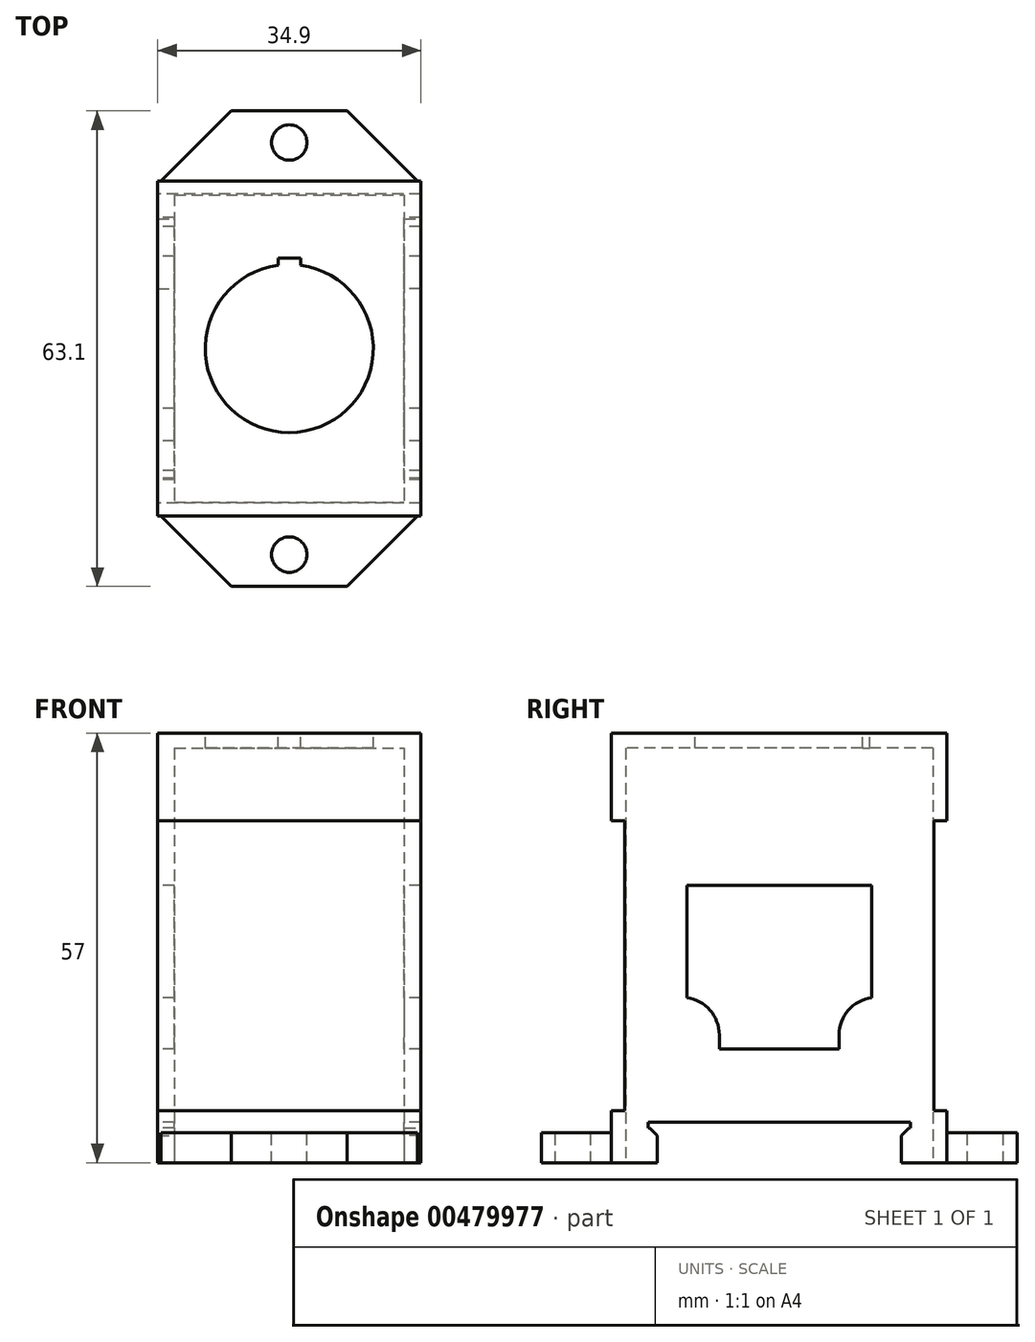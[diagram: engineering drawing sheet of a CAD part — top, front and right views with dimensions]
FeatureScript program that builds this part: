
annotation { "Feature Type Name" : "Feature", "Feature Type Description" : "" }
export const myFeature = defineFeature(function(context is Context, id is Id, definition is map)
    precondition{}
    {
        {
            var Q0;
            Q0=qCreatedBy(makeId("Top.planeOp"),FACE);
            var sketch = newSketch(context, id + "F0", { "sketchPlane" : qUnion([Q0])});
            skLineSegment(sketch, "E0.bottom", {"start": v(0, 0.4) * mm, "end": v(34.9, 0.4) * mm});
            skLineSegment(sketch, "E0.top", {"start": v(0, 44.9) * mm, "end": v(34.9, 44.9) * mm});
            skLineSegment(sketch, "E0.left", {"start": v(0, 0.4) * mm, "end": v(0, 44.9) * mm});
            skLineSegment(sketch, "E0.right", {"start": v(34.9, 0.4) * mm, "end": v(34.9, 44.9) * mm});
            skSolve(sketch);
        }
        {
            var Q0;
            Q0 = qSketchRegion(id + "F0", true);
            extrude(context, id + "F1", {"entities" : qUnion([Q0]), "depth" : 57 * mm});
        }
        {
            var Q0;
            Q0=makeQuery(id+"F1.opExtrude","CAP_FACE",FACE,{"disambiguationData":[OSD([sQuery(id+"F0.wireOp",EDGE,"E0.bottom"),sQuery(id+"F0.wireOp",EDGE,"E0.top"),sQuery(id+"F0.wireOp",EDGE,"E0.left"),sQuery(id+"F0.wireOp",EDGE,"E0.right")])],"isStart":true});
            var sketch = newSketch(context, id + "F2", { "sketchPlane" : qUnion([Q0])});
            skLineSegment(sketch, "E1.bottom", {"start": v(2.2, -43.06) * mm, "end": v(32.7, -43.06) * mm});
            skLineSegment(sketch, "E1.top", {"start": v(2.2, -2.26) * mm, "end": v(32.7, -2.26) * mm});
            skLineSegment(sketch, "E1.left", {"start": v(2.2, -43.06) * mm, "end": v(2.2, -2.26) * mm});
            skLineSegment(sketch, "E1.right", {"start": v(32.7, -43.06) * mm, "end": v(32.7, -2.26) * mm});
            skSolve(sketch);
        }
        {
            var Q0;
            Q0 = qSketchRegion(id + "F2", true);
            extrude(context, id + "F3", {"entities" : qUnion([Q0]), "operationType" : NewBodyOperationType.REMOVE, "oppositeDirection" : true, "depth" : 55 * mm});
        }
        {
            var Q0;
            Q0=makeQuery(id+"F1.opExtrude","CAP_FACE",FACE,{"disambiguationData":[OSD([sQuery(id+"F0.wireOp",EDGE,"E0.bottom"),sQuery(id+"F0.wireOp",EDGE,"E0.top"),sQuery(id+"F0.wireOp",EDGE,"E0.left"),sQuery(id+"F0.wireOp",EDGE,"E0.right")])],"isStart":false});
            var sketch = newSketch(context, id + "F4", { "sketchPlane" : qUnion([Q0])});
            skCircle(sketch, "E2", {"center": v(17.45, 22.66) * mm, "radius": 11.15 * mm});
            skLineSegment(sketch, "E3.bottom", {"start": v(18.95, 34.65) * mm, "end": v(15.95, 34.65) * mm});
            skLineSegment(sketch, "E3.top", {"start": v(18.95, 33.29) * mm, "end": v(15.95, 33.29) * mm});
            skLineSegment(sketch, "E3.left", {"start": v(18.95, 34.65) * mm, "end": v(18.95, 33.29) * mm});
            skLineSegment(sketch, "E3.right", {"start": v(15.95, 34.65) * mm, "end": v(15.95, 33.29) * mm});
            skSolve(sketch);
        }
        {
            var Q0;
            {var subQ5=sQuery(id+"F4.wireOp",EDGE,"E3.top");Q0=makeQuery(id+"F4.imprint","IMPRINT",FACE,{"disambiguationData":[TD([[makeQuery(id+"F4.imprint","IMPRINT",EDGE,{"derivedFrom":subQ5}),-1.0]])]});}
            var Q1;
            {var subQ5=sQuery(id+"F4.wireOp",EDGE,"E3.top");Q1=makeQuery(id+"F4.imprint","IMPRINT",FACE,{"disambiguationData":[TD([[makeQuery(id+"F4.imprint","IMPRINT",EDGE,{"derivedFrom":subQ5}),1.0]])]});}
            var Q2;
            {var subQ5=sQuery(id+"F4.wireOp",EDGE,"E3.bottom");Q2=makeQuery(id+"F4.imprint","IMPRINT",FACE,{"disambiguationData":[TD([[makeQuery(id+"F4.imprint","IMPRINT",EDGE,{"derivedFrom":subQ5}),1.0]])]});}
            extrude(context, id + "F5", {"entities" : qUnion([Q0, Q1, Q2]), "operationType" : NewBodyOperationType.REMOVE, "endBound" : BoundingType.THROUGH_ALL, "oppositeDirection" : true, "depth" : 25 * mm});
        }
        {
            var Q0;
            Q0=makeQuery(id+"F1.opExtrude","SWEPT_FACE",FACE,{"disambiguationData":[OSD([sQuery(id+"F0.wireOp",EDGE,"E0.left")])]});
            var sketch = newSketch(context, id + "F6", { "sketchPlane" : qUnion([Q0])});
            skLineSegment(sketch, "E4.bottom", {"start": v(-44.9, 45.4) * mm, "end": v(-43.16, 45.4) * mm});
            skLineSegment(sketch, "E4.top", {"start": v(-44.9, 6.9) * mm, "end": v(-43.16, 6.9) * mm});
            skLineSegment(sketch, "E4.left", {"start": v(-44.9, 45.4) * mm, "end": v(-44.9, 6.9) * mm});
            skLineSegment(sketch, "E4.right", {"start": v(-43.16, 45.4) * mm, "end": v(-43.16, 6.9) * mm});
            skLineSegment(sketch, "E5", {"start": v(-22.66, 57) * mm, "end": v(-22.66, 0) * mm});
            skLineSegment(sketch, "E6.MirrorCS", {"start": v(-0.4, 6.9) * mm, "end": v(-2.16, 6.9) * mm});
            skLineSegment(sketch, "E7.MirrorCS", {"start": v(-0.4, 45.4) * mm, "end": v(-2.16, 45.4) * mm});
            skLineSegment(sketch, "E8.MirrorCS", {"start": v(-2.16, 45.4) * mm, "end": v(-2.16, 6.9) * mm});
            skLineSegment(sketch, "E9.MirrorCS", {"start": v(-0.4, 45.4) * mm, "end": v(-0.4, 6.9) * mm});
            skSolve(sketch);
        }
        {
            var Q0;
            Q0 = qSketchRegion(id + "F6", true);
            extrude(context, id + "F7", {"entities" : qUnion([Q0]), "operationType" : NewBodyOperationType.REMOVE, "endBound" : BoundingType.THROUGH_ALL, "oppositeDirection" : true, "depth" : 25 * mm});
        }
        {
            var Q0;
            Q0=makeQuery(id+"F1.opExtrude","SWEPT_FACE",FACE,{"disambiguationData":[OSD([sQuery(id+"F0.wireOp",EDGE,"E0.left")])]});
            var sketch = newSketch(context, id + "F8", { "sketchPlane" : qUnion([Q0])});
            skLineSegment(sketch, "E10.bottom", {"start": v(-34.9, 36.8) * mm, "end": v(-10.4, 36.8) * mm});
            skLineSegment(sketch, "E10.top", {"start": v(-34.9, 21.9) * mm, "end": v(-10.4, 21.9) * mm});
            skLineSegment(sketch, "E10.left", {"start": v(-34.9, 36.8) * mm, "end": v(-34.9, 21.9) * mm});
            skLineSegment(sketch, "E10.right", {"start": v(-10.4, 36.8) * mm, "end": v(-10.4, 21.9) * mm});
            skLineSegment(sketch, "E11.bottom", {"start": v(-30.6, 21.9) * mm, "end": v(-14.7, 21.9) * mm});
            skLineSegment(sketch, "E11.top", {"start": v(-30.6, 15.1) * mm, "end": v(-14.7, 15.1) * mm});
            skLineSegment(sketch, "E11.left", {"start": v(-30.6, 21.9) * mm, "end": v(-30.6, 15.1) * mm});
            skLineSegment(sketch, "E11.right", {"start": v(-14.7, 21.9) * mm, "end": v(-14.7, 15.1) * mm});
            skLineSegment(sketch, "E12.bottom", {"start": v(-38.86, 0) * mm, "end": v(-6.46, 0) * mm});
            skLineSegment(sketch, "E12.top", {"start": v(-38.86, 4.6) * mm, "end": v(-6.46, 4.6) * mm});
            skLineSegment(sketch, "E12.left", {"start": v(-38.86, 0) * mm, "end": v(-38.86, 4.6) * mm});
            skLineSegment(sketch, "E12.right", {"start": v(-6.46, 0) * mm, "end": v(-6.46, 4.6) * mm});
            skLineSegment(sketch, "E13.bottom", {"start": v(-40.06, 5.4) * mm, "end": v(-5.26, 5.4) * mm});
            skLineSegment(sketch, "E13.top", {"start": v(-40.06, 4.6) * mm, "end": v(-5.26, 4.6) * mm});
            skLineSegment(sketch, "E13.left", {"start": v(-40.06, 5.4) * mm, "end": v(-40.06, 4.6) * mm});
            skLineSegment(sketch, "E13.right", {"start": v(-5.26, 5.4) * mm, "end": v(-5.26, 4.6) * mm});
            skSolve(sketch);
        }
        {
            var Q0;
            Q0 = qSketchRegion(id + "F8", true);
            extrude(context, id + "F9", {"entities" : qUnion([Q0]), "operationType" : NewBodyOperationType.REMOVE, "endBound" : BoundingType.THROUGH_ALL, "oppositeDirection" : true, "depth" : 25 * mm});
        }
        {
            var Q0;
            {var subQ2=sQuery(id+"F0.wireOp",EDGE,"E0.bottom");Q0=makeQuery(id+"F7.boolean.opBoolean","SPLIT",FACE,{"disambiguationData":[TD([makeQuery(id+"F7.opExtrude","SWEPT_FACE",FACE,{"disambiguationData":[OSD([sQuery(id+"F6.wireOp",EDGE,"E6.MirrorCS")])]})])],"derivedFrom":makeQuery(id+"F1.opExtrude","SWEPT_FACE",FACE,{"disambiguationData":[OSD([subQ2])]})});}
            var sketch = newSketch(context, id + "F10", { "sketchPlane" : qUnion([Q0])});
            skLineSegment(sketch, "E14.bottom", {"start": v(0.45, 0) * mm, "end": v(34.45, 0) * mm});
            skLineSegment(sketch, "E14.top", {"start": v(0.45, 4) * mm, "end": v(34.45, 4) * mm});
            skLineSegment(sketch, "E14.left", {"start": v(0.45, 0) * mm, "end": v(0.45, 4) * mm});
            skLineSegment(sketch, "E14.right", {"start": v(34.45, 0) * mm, "end": v(34.45, 4) * mm});
            skSolve(sketch);
        }
        {
            var Q0;
            Q0 = qSketchRegion(id + "F10", true);
            extrude(context, id + "F11", {"entities" : qUnion([Q0]), "operationType" : NewBodyOperationType.ADD, "depth" : 9.3 * mm});
        }
        {
            var Q0;
            {var subQ2=sQuery(id+"F0.wireOp",EDGE,"E0.top");Q0=makeQuery(id+"F7.boolean.opBoolean","SPLIT",FACE,{"disambiguationData":[TD([makeQuery(id+"F7.opExtrude","SWEPT_FACE",FACE,{"disambiguationData":[OSD([sQuery(id+"F6.wireOp",EDGE,"E4.top")])]})])],"derivedFrom":makeQuery(id+"F1.opExtrude","SWEPT_FACE",FACE,{"disambiguationData":[OSD([subQ2])]})});}
            var sketch = newSketch(context, id + "F12", { "sketchPlane" : qUnion([Q0])});
            skLineSegment(sketch, "E15.bottom", {"start": v(-34.45, 0) * mm, "end": v(-0.45, 0) * mm});
            skLineSegment(sketch, "E15.top", {"start": v(-34.45, 4) * mm, "end": v(-0.45, 4) * mm});
            skLineSegment(sketch, "E15.left", {"start": v(-34.45, 0) * mm, "end": v(-34.45, 4) * mm});
            skLineSegment(sketch, "E15.right", {"start": v(-0.45, 0) * mm, "end": v(-0.45, 4) * mm});
            skSolve(sketch);
        }
        {
            var Q0;
            Q0 = qSketchRegion(id + "F12", true);
            extrude(context, id + "F13", {"entities" : qUnion([Q0]), "operationType" : NewBodyOperationType.ADD, "depth" : 9.3 * mm});
        }
        {
            var Q0;
            Q0=makeQuery(id+"F13.opExtrude","CAP_EDGE",EDGE,{"disambiguationData":[OSD([sQuery(id+"F12.wireOp",EDGE,"E15.left")])],"isStart":false});
            var Q1;
            Q1=makeQuery(id+"F13.opExtrude","CAP_EDGE",EDGE,{"disambiguationData":[OSD([sQuery(id+"F12.wireOp",EDGE,"E15.right")])],"isStart":false});
            var Q2;
            Q2=makeQuery(id+"F11.opExtrude","CAP_EDGE",EDGE,{"disambiguationData":[OSD([sQuery(id+"F10.wireOp",EDGE,"E14.right")])],"isStart":false});
            var Q3;
            Q3=makeQuery(id+"F11.opExtrude","CAP_EDGE",EDGE,{"disambiguationData":[OSD([sQuery(id+"F10.wireOp",EDGE,"E14.left")])],"isStart":false});
            chamfer(context, id + "F14", {"entities" : qUnion([Q0, Q1, Q2, Q3]), "width" : 9.3 * mm, "tangentPropagation" : true});
        }
        {
            var Q0;
            {var subQ0=sQuery(id+"F8.wireOp",EDGE,"E12.left");var subQ1=sQuery(id+"F8.wireOp",EDGE,"E13.top");Q0=makeQuery(id+"F9.boolean.opBoolean","COPY",EDGE,{"disambiguationData":[TD([makeQuery(id+"F1.opExtrude","SWEPT_FACE",FACE,{"disambiguationData":[OSD([sQuery(id+"F0.wireOp",EDGE,"E0.left")])]})])],"derivedFrom":makeQuery(id+"F9.opExtrude","SWEPT_EDGE",EDGE,{"disambiguationData":[OSD([subQ0,subQ1])]})});}
            var Q1;
            {var subQ0=sQuery(id+"F8.wireOp",EDGE,"E12.right");var subQ1=sQuery(id+"F8.wireOp",EDGE,"E13.top");Q1=makeQuery(id+"F9.boolean.opBoolean","COPY",EDGE,{"disambiguationData":[TD([makeQuery(id+"F1.opExtrude","SWEPT_FACE",FACE,{"disambiguationData":[OSD([sQuery(id+"F0.wireOp",EDGE,"E0.left")])]})])],"derivedFrom":makeQuery(id+"F9.opExtrude","SWEPT_EDGE",EDGE,{"disambiguationData":[OSD([subQ0,subQ1])]})});}
            var Q2;
            {var subQ0=sQuery(id+"F8.wireOp",EDGE,"E12.right");var subQ1=sQuery(id+"F8.wireOp",EDGE,"E13.top");Q2=makeQuery(id+"F9.boolean.opBoolean","COPY",EDGE,{"disambiguationData":[TD([makeQuery(id+"F1.opExtrude","SWEPT_FACE",FACE,{"disambiguationData":[OSD([sQuery(id+"F0.wireOp",EDGE,"E0.right")])]})])],"derivedFrom":makeQuery(id+"F9.opExtrude","SWEPT_EDGE",EDGE,{"disambiguationData":[OSD([subQ0,subQ1])]})});}
            var Q3;
            {var subQ0=sQuery(id+"F8.wireOp",EDGE,"E12.left");var subQ1=sQuery(id+"F8.wireOp",EDGE,"E13.top");Q3=makeQuery(id+"F9.boolean.opBoolean","COPY",EDGE,{"disambiguationData":[TD([makeQuery(id+"F1.opExtrude","SWEPT_FACE",FACE,{"disambiguationData":[OSD([sQuery(id+"F0.wireOp",EDGE,"E0.right")])]})])],"derivedFrom":makeQuery(id+"F9.opExtrude","SWEPT_EDGE",EDGE,{"disambiguationData":[OSD([subQ0,subQ1])]})});}
            chamfer(context, id + "F15", {"entities" : qUnion([Q0, Q1, Q2, Q3]), "width" : 1 * mm, "tangentPropagation" : true});
        }
        {
            var Q0;
            Q0=makeQuery(id+"F11.opExtrude","SWEPT_FACE",FACE,{"disambiguationData":[OSD([sQuery(id+"F10.wireOp",EDGE,"E14.top")])]});
            var sketch = newSketch(context, id + "F16", { "sketchPlane" : qUnion([Q0])});
            skCircle(sketch, "E16", {"center": v(17.45, -4.7) * mm, "radius": 2.35 * mm});
            skCircle(sketch, "E17", {"center": v(17.45, 50) * mm, "radius": 2.35 * mm});
            skSolve(sketch);
        }
        {
            var Q0;
            Q0 = qSketchRegion(id + "F16", true);
            extrude(context, id + "F17", {"entities" : qUnion([Q0]), "operationType" : NewBodyOperationType.REMOVE, "endBound" : BoundingType.THROUGH_ALL, "oppositeDirection" : true, "depth" : 25 * mm});
        }
        {
            var Q0;
            {var subQ0=sQuery(id+"F8.wireOp",EDGE,"E10.top");var subQ1=sQuery(id+"F8.wireOp",EDGE,"E11.left");var subQ2=sQuery(id+"F8.wireOp",EDGE,"E11.bottom");Q0=makeQuery(id+"F9.boolean.opBoolean","COPY",EDGE,{"disambiguationData":[TD([makeQuery(id+"F1.opExtrude","SWEPT_FACE",FACE,{"disambiguationData":[OSD([sQuery(id+"F0.wireOp",EDGE,"E0.left")])]})])],"derivedFrom":makeQuery(id+"F9.opExtrude","SWEPT_EDGE",EDGE,{"disambiguationData":[OSD([subQ0,subQ2,subQ1])]})});}
            var Q1;
            {var subQ0=sQuery(id+"F8.wireOp",EDGE,"E10.top");var subQ1=sQuery(id+"F8.wireOp",EDGE,"E11.right");var subQ2=sQuery(id+"F8.wireOp",EDGE,"E11.bottom");Q1=makeQuery(id+"F9.boolean.opBoolean","COPY",EDGE,{"disambiguationData":[TD([makeQuery(id+"F1.opExtrude","SWEPT_FACE",FACE,{"disambiguationData":[OSD([sQuery(id+"F0.wireOp",EDGE,"E0.left")])]})])],"derivedFrom":makeQuery(id+"F9.opExtrude","SWEPT_EDGE",EDGE,{"disambiguationData":[OSD([subQ0,subQ2,subQ1])]})});}
            var Q2;
            {var subQ0=sQuery(id+"F8.wireOp",EDGE,"E10.top");var subQ1=sQuery(id+"F8.wireOp",EDGE,"E11.right");var subQ2=sQuery(id+"F8.wireOp",EDGE,"E11.bottom");Q2=makeQuery(id+"F9.boolean.opBoolean","COPY",EDGE,{"disambiguationData":[TD([makeQuery(id+"F1.opExtrude","SWEPT_FACE",FACE,{"disambiguationData":[OSD([sQuery(id+"F0.wireOp",EDGE,"E0.right")])]})])],"derivedFrom":makeQuery(id+"F9.opExtrude","SWEPT_EDGE",EDGE,{"disambiguationData":[OSD([subQ0,subQ2,subQ1])]})});}
            var Q3;
            {var subQ0=sQuery(id+"F8.wireOp",EDGE,"E10.top");var subQ1=sQuery(id+"F8.wireOp",EDGE,"E11.left");var subQ2=sQuery(id+"F8.wireOp",EDGE,"E11.bottom");Q3=makeQuery(id+"F9.boolean.opBoolean","COPY",EDGE,{"disambiguationData":[TD([makeQuery(id+"F1.opExtrude","SWEPT_FACE",FACE,{"disambiguationData":[OSD([sQuery(id+"F0.wireOp",EDGE,"E0.right")])]})])],"derivedFrom":makeQuery(id+"F9.opExtrude","SWEPT_EDGE",EDGE,{"disambiguationData":[OSD([subQ0,subQ2,subQ1])]})});}
            fillet(context, id + "F18", {"entities" : qUnion([Q0, Q1, Q2, Q3]), "radius" : 5 * mm, "tangentPropagation" : true, "allowEdgeOverflow" : false});
        }
    });
